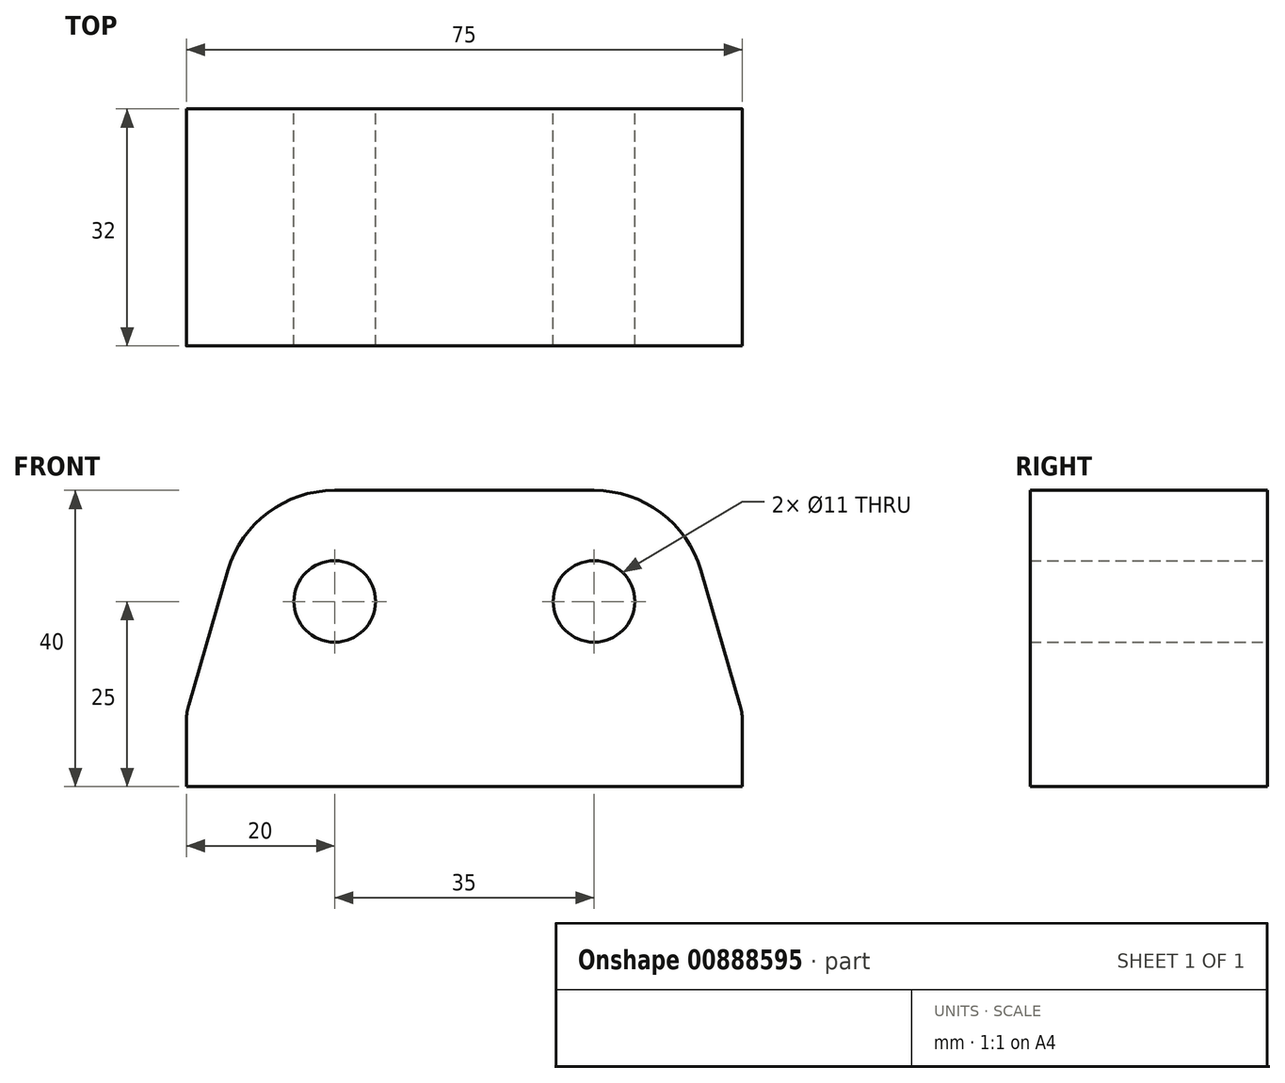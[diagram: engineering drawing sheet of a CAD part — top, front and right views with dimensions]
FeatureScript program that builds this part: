
annotation { "Feature Type Name" : "Feature", "Feature Type Description" : "" }
export const myFeature = defineFeature(function(context is Context, id is Id, definition is map)
    precondition{}
    {
        {
            var Q0;
            Q0=qCreatedBy(makeId("Front.planeOp"),FACE);
            var sketch = newSketch(context, id + "F0", { "sketchPlane" : qUnion([Q0])});
            skCircle(sketch, "E0", {"center": v(0, 0) * mm, "radius": 5.5 * mm});
            skArc(sketch, "E1", {"start": v(10.73, 10.49) * mm, "mid": v(-3.64, 14.55) * mm, "end": v(-14.4, 4.2) * mm});
            skLineSegment(sketch, "E2", {"start": v(0, -25) * mm, "end": v(-20, -25) * mm});
            skLineSegment(sketch, "E3", {"start": v(0, -25) * mm, "end": v(20, -25) * mm});
            skLineSegment(sketch, "E4", {"start": v(-20, -25) * mm, "end": v(-20, -16.07) * mm});
            skLineSegment(sketch, "E5", {"start": v(-19.7, -13.97) * mm, "end": v(-14.4, 4.2) * mm});
            skLineSegment(sketch, "E6", {"start": v(0, 0) * mm, "end": v(35, 0) * mm});
            skArc(sketch, "E7", {"start": v(49.4, 4.2) * mm, "mid": v(38.64, 14.55) * mm, "end": v(24.27, 10.49) * mm});
            skLineSegment(sketch, "E8", {"start": v(18.91, 8.23) * mm, "end": v(16.09, 8.23) * mm});
            skLineSegment(sketch, "E9", {"start": v(50, -25) * mm, "end": v(55, -25) * mm});
            skLineSegment(sketch, "E10", {"start": v(55, -25) * mm, "end": v(55, -16.07) * mm});
            skLineSegment(sketch, "E11", {"start": v(54.7, -13.97) * mm, "end": v(49.4, 4.2) * mm});
            skPoint(sketch, "E12.orphan", {"position": v(50, 0) * mm});
            skPoint(sketch, "E13.orphan", {"position": v(20, -15) * mm});
            skPoint(sketch, "E14.end.orphan", {"position": v(14.4, 4.2) * mm});
            skPoint(sketch, "E15.end.orphan", {"position": v(15, -25) * mm});
            skLineSegment(sketch, "E16", {"start": v(20, -25) * mm, "end": v(55, -25) * mm});
            skCircle(sketch, "E17", {"center": v(35, 0) * mm, "radius": 5.5 * mm});
            skPoint(sketch, "E18.visualSharp", {"position": v(22.46, 8.23) * mm});
            skArc(sketch, "E18.filletArc", {"start": v(18.91, 8.23) * mm, "mid": v(21.82, 8.82) * mm, "end": v(24.27, 10.49) * mm});
            skPoint(sketch, "E19.visualSharp", {"position": v(12.54, 8.23) * mm});
            skArc(sketch, "E19.filletArc", {"start": v(10.73, 10.49) * mm, "mid": v(13.18, 8.82) * mm, "end": v(16.09, 8.23) * mm});
            skPoint(sketch, "E20.visualSharp", {"position": v(55, -15) * mm});
            skArc(sketch, "E20.filletArc", {"start": v(55, -16.07) * mm, "mid": v(54.92, -15.01) * mm, "end": v(54.7, -13.97) * mm});
            skPoint(sketch, "E21.visualSharp", {"position": v(-20, -15) * mm});
            skArc(sketch, "E21.filletArc", {"start": v(-19.7, -13.97) * mm, "mid": v(-19.92, -15.01) * mm, "end": v(-20, -16.07) * mm});
            skSolve(sketch);
        }
        {
            var Q0;
            Q0=makeQuery(id+"F0.imprint","IMPRINT",FACE,{"disambiguationData":[TD([[makeQuery(id+"F0.imprint","IMPRINT",EDGE,{"derivedFrom":sQuery(id+"F0.wireOp",EDGE,"E0")}),-1.0]])]});
            var Q1;
            {var subQ0=sQuery(id+"F0.wireOp",EDGE,"E2");Q1=makeQuery(id+"F0.imprint","IMPRINT",FACE,{"disambiguationData":[TD([[makeQuery(id+"F0.imprint","IMPRINT",EDGE,{"derivedFrom":subQ0}),-1.0]])]});}
            var Q2;
            {var subQ0=sQuery(id+"F0.wireOp",EDGE,"E3");Q2=makeQuery(id+"F0.imprint","IMPRINT",FACE,{"disambiguationData":[TD([[makeQuery(id+"F0.imprint","IMPRINT",EDGE,{"derivedFrom":subQ0}),1.0]])]});}
            extrude(context, id + "F1", {"entities" : qUnion([Q0, Q1, Q2]), "depth" : 32 * mm, "offsetDistance" : 25 * mm});
        }
        {
            var Q0;
            Q0=makeQuery(id+"F1.opExtrude","CAP_FACE",FACE,{"disambiguationData":[OSD([sQuery(id+"F0.wireOp",EDGE,"E0"),sQuery(id+"F0.wireOp",EDGE,"E1"),sQuery(id+"F0.wireOp",EDGE,"E2"),sQuery(id+"F0.wireOp",EDGE,"E3"),sQuery(id+"F0.wireOp",EDGE,"E4"),sQuery(id+"F0.wireOp",EDGE,"E5"),sQuery(id+"F0.wireOp",EDGE,"E7"),sQuery(id+"F0.wireOp",EDGE,"E8"),sQuery(id+"F0.wireOp",EDGE,"E10"),sQuery(id+"F0.wireOp",EDGE,"E11"),sQuery(id+"F0.wireOp",EDGE,"E16"),sQuery(id+"F0.wireOp",EDGE,"E17"),sQuery(id+"F0.wireOp",EDGE,"E18.filletArc"),sQuery(id+"F0.wireOp",EDGE,"E19.filletArc"),sQuery(id+"F0.wireOp",EDGE,"E20.filletArc"),sQuery(id+"F0.wireOp",EDGE,"E21.filletArc")])],"isStart":true});
            var sketch = newSketch(context, id + "F2", { "sketchPlane" : qUnion([Q0])});
            skLineSegment(sketch, "E22", {"start": v(0, 0) * mm, "end": v(0, 15) * mm});
            skLineSegment(sketch, "E23", {"start": v(0, 15) * mm, "end": v(-35, 15) * mm});
            skLineSegment(sketch, "E24", {"start": v(-35, 15) * mm, "end": v(-18.97, 5.21) * mm});
            skLineSegment(sketch, "E25", {"start": v(-18.97, 5.21) * mm, "end": v(0, 15) * mm});
            skSolve(sketch);
        }
        {
            var Q0;
            Q0 = qSketchRegion(id + "F2", true);
            extrude(context, id + "F3", {"entities" : qUnion([Q0]), "operationType" : NewBodyOperationType.ADD, "oppositeDirection" : true, "depth" : 32 * mm, "offsetDistance" : 25 * mm});
        }
    });
